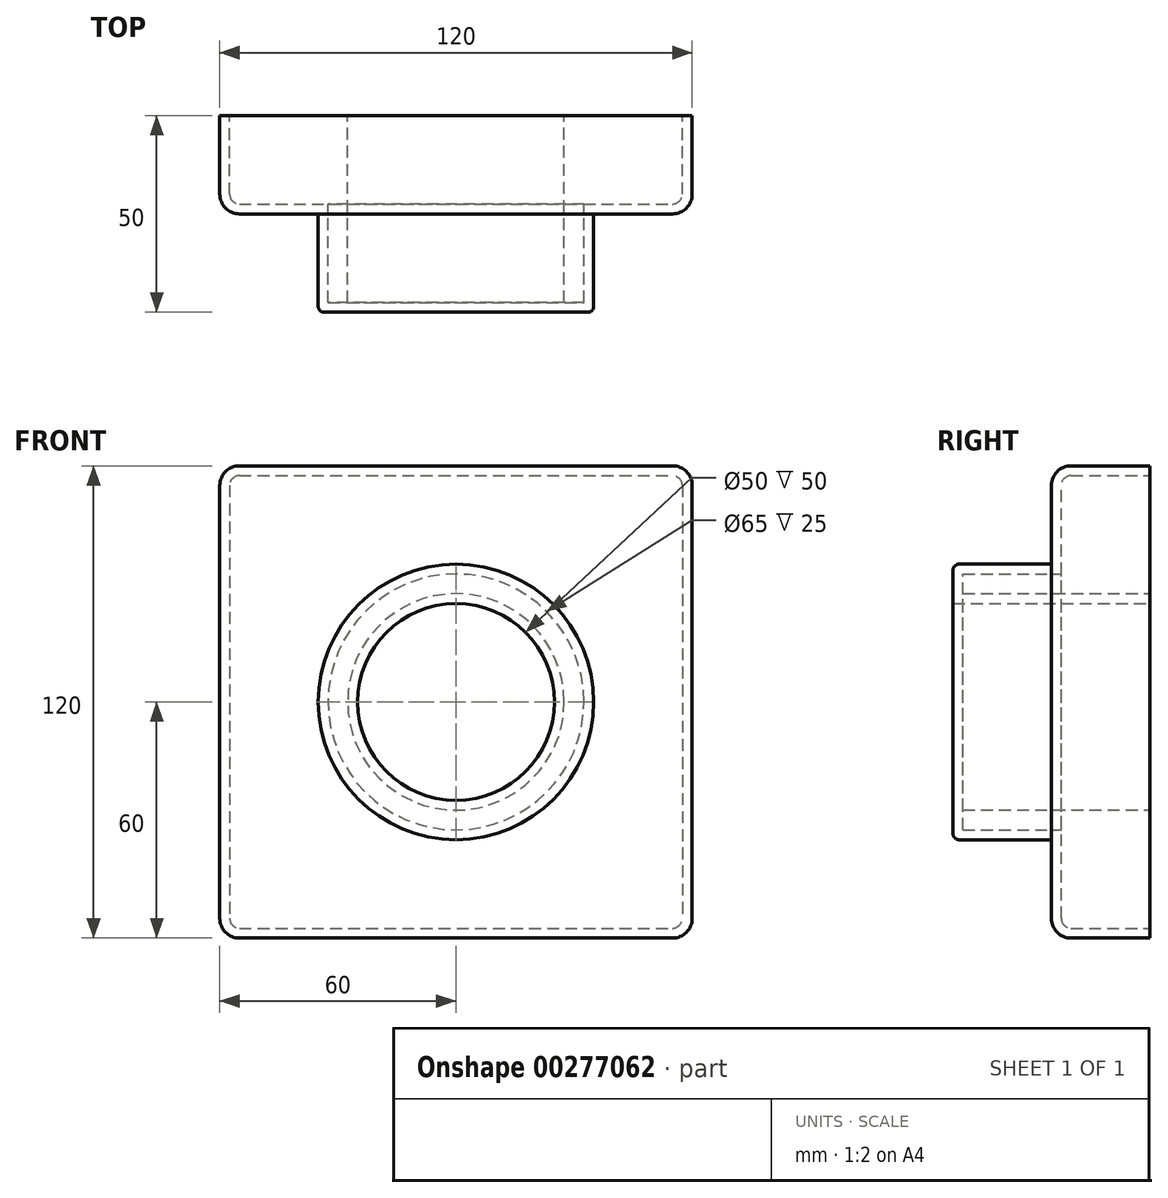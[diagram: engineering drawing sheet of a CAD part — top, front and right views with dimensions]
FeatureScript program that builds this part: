
annotation { "Feature Type Name" : "Feature", "Feature Type Description" : "" }
export const myFeature = defineFeature(function(context is Context, id is Id, definition is map)
    precondition{}
    {
        {
            var Q0;
            Q0=qCreatedBy(makeId("Front.planeOp"),FACE);
            var sketch = newSketch(context, id + "F0", { "sketchPlane" : qUnion([Q0])});
            skLineSegment(sketch, "E0.bottom", {"start": v(-60, 60) * mm, "end": v(60, 60) * mm});
            skLineSegment(sketch, "E0.top", {"start": v(-60, -60) * mm, "end": v(60, -60) * mm});
            skLineSegment(sketch, "E0.left", {"start": v(-60, 60) * mm, "end": v(-60, -60) * mm});
            skLineSegment(sketch, "E0.right", {"start": v(60, 60) * mm, "end": v(60, -60) * mm});
            skPoint(sketch, "E0.middle", {"position": v(0, 0) * mm});
            skSolve(sketch);
        }
        {
            var Q0;
            Q0 = qSketchRegion(id + "F0", true);
            extrude(context, id + "F1", {"entities" : qUnion([Q0]), "depth" : 25 * mm});
        }
        {
            var Q0;
            Q0=makeQuery(id+"F1.opExtrude","CAP_FACE",FACE,{"disambiguationData":[OSD([sQuery(id+"F0.wireOp",EDGE,"E0.bottom"),sQuery(id+"F0.wireOp",EDGE,"E0.top"),sQuery(id+"F0.wireOp",EDGE,"E0.left"),sQuery(id+"F0.wireOp",EDGE,"E0.right")])],"isStart":false});
            var sketch = newSketch(context, id + "F2", { "sketchPlane" : qUnion([Q0])});
            skCircle(sketch, "E1", {"center": v(0, 0) * mm, "radius": 25 * mm});
            skCircle(sketch, "E2", {"center": v(0, 0) * mm, "radius": 35 * mm});
            skSolve(sketch);
        }
        {
            var Q0;
            Q0 = qSketchRegion(id + "F2", true);
            extrude(context, id + "F3", {"entities" : qUnion([Q0]), "operationType" : NewBodyOperationType.ADD, "depth" : 25 * mm});
        }
        {
            var Q0;
            Q0=makeQuery(id+"F1.opExtrude","CAP_EDGE",EDGE,{"disambiguationData":[OSD([sQuery(id+"F0.wireOp",EDGE,"E0.bottom")])],"isStart":false});
            var Q1;
            Q1=makeQuery(id+"F1.opExtrude","CAP_EDGE",EDGE,{"disambiguationData":[OSD([sQuery(id+"F0.wireOp",EDGE,"E0.left")])],"isStart":false});
            var Q2;
            Q2=makeQuery(id+"F1.opExtrude","CAP_EDGE",EDGE,{"disambiguationData":[OSD([sQuery(id+"F0.wireOp",EDGE,"E0.right")])],"isStart":false});
            var Q3;
            Q3=makeQuery(id+"F1.opExtrude","CAP_EDGE",EDGE,{"disambiguationData":[OSD([sQuery(id+"F0.wireOp",EDGE,"E0.top")])],"isStart":false});
            var Q4;
            Q4=makeQuery(id+"F1.opExtrude","SWEPT_EDGE",EDGE,{"disambiguationData":[OSD([sQuery(id+"F0.wireOp",EDGE,"E0.bottom"),sQuery(id+"F0.wireOp",EDGE,"E0.right")])]});
            var Q5;
            Q5=makeQuery(id+"F1.opExtrude","SWEPT_EDGE",EDGE,{"disambiguationData":[OSD([sQuery(id+"F0.wireOp",EDGE,"E0.top"),sQuery(id+"F0.wireOp",EDGE,"E0.right")])]});
            var Q6;
            Q6=makeQuery(id+"F1.opExtrude","SWEPT_EDGE",EDGE,{"disambiguationData":[OSD([sQuery(id+"F0.wireOp",EDGE,"E0.top"),sQuery(id+"F0.wireOp",EDGE,"E0.left")])]});
            var Q7;
            Q7=makeQuery(id+"F1.opExtrude","SWEPT_EDGE",EDGE,{"disambiguationData":[OSD([sQuery(id+"F0.wireOp",EDGE,"E0.bottom"),sQuery(id+"F0.wireOp",EDGE,"E0.left")])]});
            var Q8;
            Q8=makeQuery(id+"F3.opExtrude","CAP_EDGE",EDGE,{"disambiguationData":[OSD([sQuery(id+"F2.wireOp",EDGE,"E2")])],"isStart":true});
            fillet(context, id + "F4", {"entities" : qUnion([Q0, Q1, Q2, Q3, Q4, Q5, Q6, Q7, Q8]), "radius" : 5 * mm, "tangentPropagation" : true, "allowEdgeOverflow" : false});
        }
        {
            var Q0;
            Q0=makeQuery(id+"F3.opExtrude","CAP_EDGE",EDGE,{"disambiguationData":[OSD([sQuery(id+"F2.wireOp",EDGE,"E2")])],"isStart":false});
            fillet(context, id + "F5", {"entities" : qUnion([Q0]), "radius" : 1.5 * mm, "tangentPropagation" : true, "allowEdgeOverflow" : false});
        }
        {
            var Q0;
            Q0=makeQuery(id+"F1.opExtrude","CAP_FACE",FACE,{"disambiguationData":[OSD([sQuery(id+"F0.wireOp",EDGE,"E0.bottom"),sQuery(id+"F0.wireOp",EDGE,"E0.top"),sQuery(id+"F0.wireOp",EDGE,"E0.left"),sQuery(id+"F0.wireOp",EDGE,"E0.right")])],"isStart":true});
            var sketch = newSketch(context, id + "F6", { "sketchPlane" : qUnion([Q0])});
            skCircle(sketch, "E3", {"center": v(0, 0) * mm, "radius": 25 * mm});
            skSolve(sketch);
        }
        {
            var Q0;
            Q0 = qSketchRegion(id + "F6", true);
            extrude(context, id + "F7", {"entities" : qUnion([Q0]), "operationType" : NewBodyOperationType.REMOVE, "endBound" : BoundingType.THROUGH_ALL, "oppositeDirection" : true, "depth" : 25 * mm});
        }
        {
            var Q0;
            Q0=makeQuery(id+"F1.opExtrude","CAP_FACE",FACE,{"disambiguationData":[OSD([sQuery(id+"F0.wireOp",EDGE,"E0.bottom"),sQuery(id+"F0.wireOp",EDGE,"E0.top"),sQuery(id+"F0.wireOp",EDGE,"E0.left"),sQuery(id+"F0.wireOp",EDGE,"E0.right")])],"isStart":true});
            shell(context, id + "F8", {"entities" : qUnion([Q0]), "thickness" : 2.5 * mm});
        }
    });
